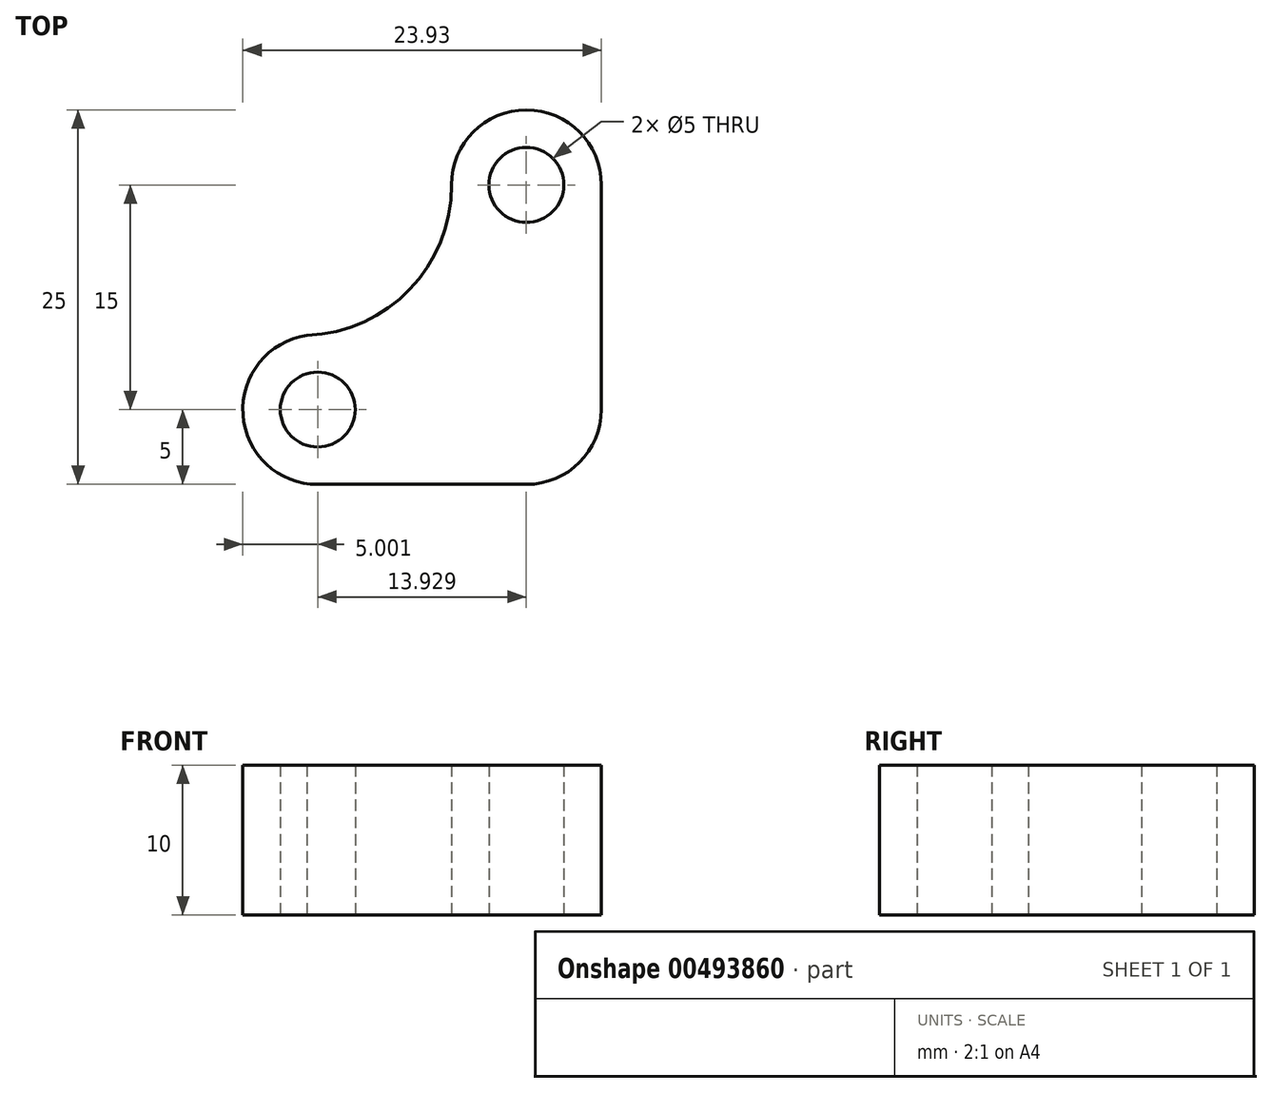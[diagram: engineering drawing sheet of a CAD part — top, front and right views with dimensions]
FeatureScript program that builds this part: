
annotation { "Feature Type Name" : "Feature", "Feature Type Description" : "" }
export const myFeature = defineFeature(function(context is Context, id is Id, definition is map)
    precondition{}
    {
        {
            var Q0;
            Q0=qCreatedBy(makeId("Top.planeOp"),FACE);
            var sketch = newSketch(context, id + "F0", { "sketchPlane" : qUnion([Q0])});
            skCircle(sketch, "E0", {"center": v(0, 0) * mm, "radius": 5 * mm});
            skCircle(sketch, "E1", {"center": v(0, 15) * mm, "radius": 5 * mm});
            skCircle(sketch, "E2", {"center": v(-13.93, 0) * mm, "radius": 5 * mm});
            skCircle(sketch, "E3", {"center": v(0, 15) * mm, "radius": 2.5 * mm});
            skCircle(sketch, "E4", {"center": v(-13.93, 0) * mm, "radius": 2.5 * mm});
            skLineSegment(sketch, "E5", {"start": v(-13.93, -5) * mm, "end": v(0, -5) * mm});
            skLineSegment(sketch, "E6", {"start": v(5, 0) * mm, "end": v(5, 15) * mm});
            skArc(sketch, "E7", {"start": v(-14.64, 4.95) * mm, "mid": v(-7.78, 8.02) * mm, "end": v(-5, 15) * mm});
            skPoint(sketch, "E7.first.point", {"position": v(-5, 15) * mm});
            skPoint(sketch, "E7.second.point", {"position": v(-24.72, 17.3) * mm});
            skPoint(sketch, "E7.third.point", {"position": v(-13.93, 5) * mm});
            skSolve(sketch);
        }
        {
            var Q0;
            {var subQ0=sQuery(id+"F0.wireOp",EDGE,"E5");Q0=makeQuery(id+"F0.imprint","IMPRINT",FACE,{"disambiguationData":[TD([[makeQuery(id+"F0.imprint","IMPRINT",EDGE,{"derivedFrom":subQ0}),1.0]])]});}
            var Q1;
            Q1=makeQuery(id+"F0.imprint","IMPRINT",FACE,{"disambiguationData":[TD([[makeQuery(id+"F0.imprint","IMPRINT",EDGE,{"derivedFrom":sQuery(id+"F0.wireOp",EDGE,"E4")}),-1.0]])]});
            var Q2;
            {var subQ0=sQuery(id+"F0.wireOp",EDGE,"E0");var subQ1=makeQuery(id+"F0.imprint","INTERSECT",VERTEX,{"derivedFrom":[subQ0,sQuery(id+"F0.wireOp",EDGE,"E5")]});Q2=makeQuery(id+"F0.imprint","IMPRINT",FACE,{"disambiguationData":[TD([[makeQuery(id+"F0.imprint","IMPRINT",EDGE,{"disambiguationData":[TD([[subQ1,1.0]])],"derivedFrom":subQ0}),1.0]])]});}
            var Q3;
            Q3=makeQuery(id+"F0.imprint","IMPRINT",FACE,{"disambiguationData":[TD([[makeQuery(id+"F0.imprint","IMPRINT",EDGE,{"derivedFrom":sQuery(id+"F0.wireOp",EDGE,"E3")}),-1.0]])]});
            extrude(context, id + "F1", {"entities" : qUnion([Q0, Q1, Q2, Q3]), "depth" : 10 * mm});
        }
    });
